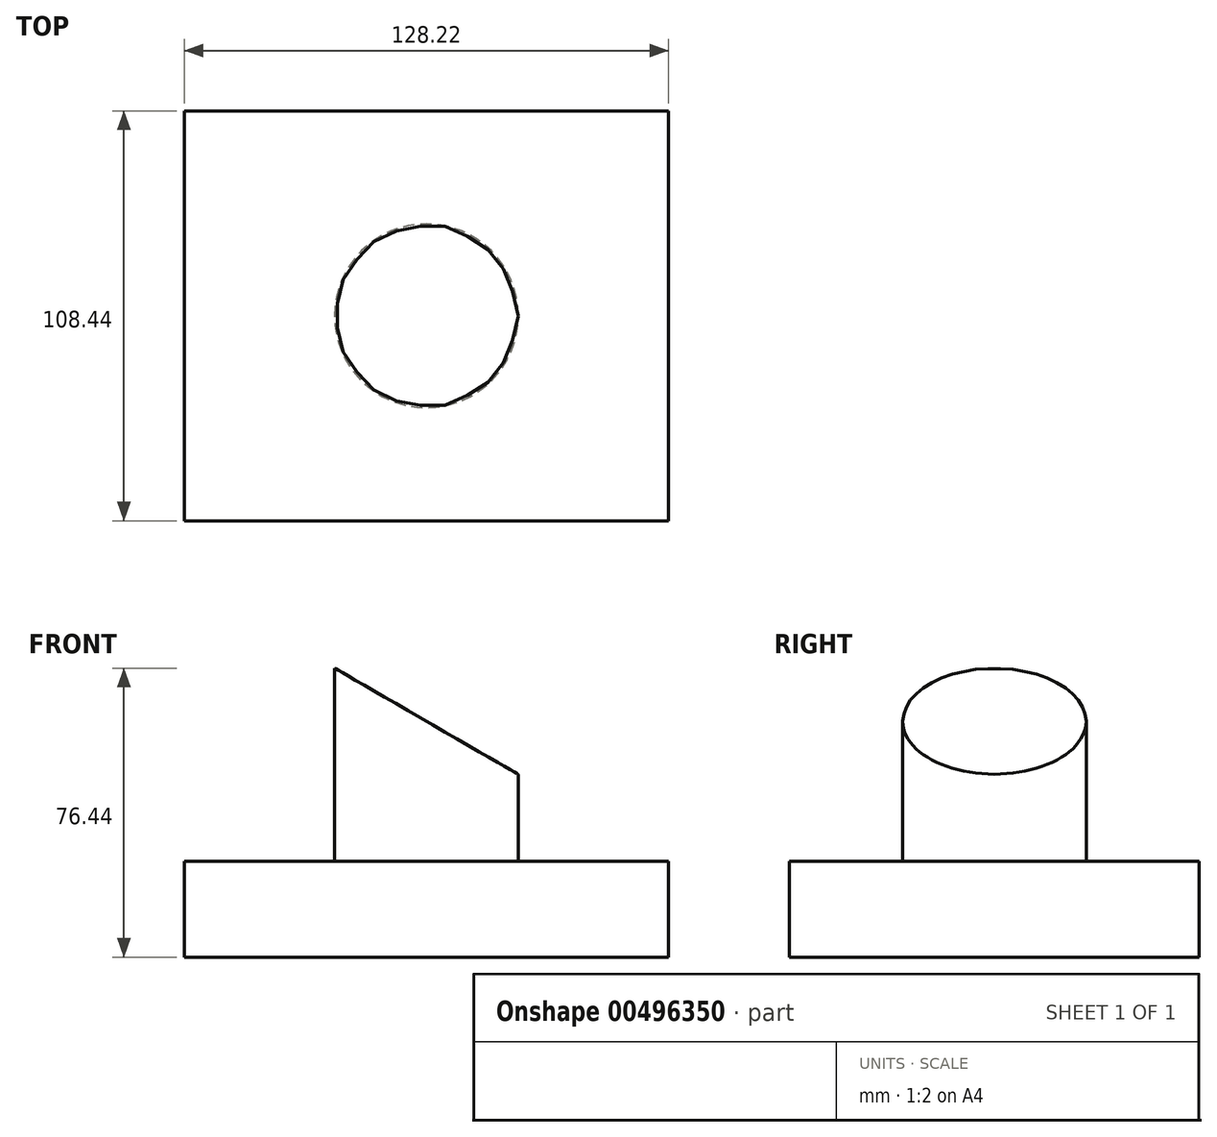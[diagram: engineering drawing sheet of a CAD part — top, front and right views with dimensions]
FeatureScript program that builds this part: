
annotation { "Feature Type Name" : "Feature", "Feature Type Description" : "" }
export const myFeature = defineFeature(function(context is Context, id is Id, definition is map)
    precondition{}
    {
        {
            var Q0;
            Q0=qCreatedBy(makeId("Top.planeOp"),FACE);
            var sketch = newSketch(context, id + "F0", { "sketchPlane" : qUnion([Q0])});
            skLineSegment(sketch, "E0.bottom", {"start": v(-64.1, -54.22) * mm, "end": v(64.1, -54.22) * mm});
            skLineSegment(sketch, "E0.top", {"start": v(-64.1, 54.22) * mm, "end": v(64.1, 54.22) * mm});
            skLineSegment(sketch, "E0.left", {"start": v(-64.1, -54.22) * mm, "end": v(-64.1, 54.22) * mm});
            skLineSegment(sketch, "E0.right", {"start": v(64.1, -54.22) * mm, "end": v(64.1, 54.22) * mm});
            skPoint(sketch, "E0.middle", {"position": v(0, 0) * mm});
            skSolve(sketch);
        }
        {
            var Q0;
            Q0=makeQuery(id+"F0.imprint","IMPRINT",FACE,{"disambiguationData":[TD([[makeQuery(id+"F0.imprint","IMPRINT",EDGE,{"derivedFrom":sQuery(id+"F0.wireOp",EDGE,"E0.bottom")}),1.0]])]});
            extrude(context, id + "F1", {"entities" : qUnion([Q0]), "depth" : 25.4 * mm});
        }
        {
            var Q0;
            Q0=makeQuery(id+"F1.opExtrude","CAP_FACE",FACE,{"disambiguationData":[OSD([sQuery(id+"F0.wireOp",EDGE,"E0.bottom"),sQuery(id+"F0.wireOp",EDGE,"E0.top"),sQuery(id+"F0.wireOp",EDGE,"E0.left"),sQuery(id+"F0.wireOp",EDGE,"E0.right")])],"isStart":false});
            var sketch = newSketch(context, id + "F2", { "sketchPlane" : qUnion([Q0])});
            skCircle(sketch, "E1", {"center": v(0, 0) * mm, "radius": 24.3 * mm});
            skSolve(sketch);
        }
        {
            var Q0;
            Q0=makeQuery(id+"F1.opExtrude","CAP_EDGE",EDGE,{"disambiguationData":[OSD([sQuery(id+"F0.wireOp",EDGE,"E0.right")])],"isStart":false});
            cPlane(context, id + "F3", {"entities" : qUnion([Q0]), "cplaneType" : CPlaneType.LINE_ANGLE, "offset" : 25.4 * mm, "angle" : 30 * degree, "width" : 152.4 * mm, "height" : 152.4 * mm});
        }
        {
            var Q0;
            Q0=makeQuery(id+"F2.imprint","IMPRINT",FACE,{"disambiguationData":[TD([[makeQuery(id+"F2.imprint","IMPRINT",EDGE,{"derivedFrom":sQuery(id+"F2.wireOp",EDGE,"E1")}),1.0]])]});
            var Q1;
            Q1=qCreatedBy(id+"F3.planeOp",FACE);
            extrude(context, id + "F4", {"entities" : qUnion([Q0]), "operationType" : NewBodyOperationType.ADD, "endBound" : BoundingType.UP_TO_SURFACE, "endBoundEntityFace" : qUnion([Q1]), "depth" : 50.8 * mm});
        }
    });
